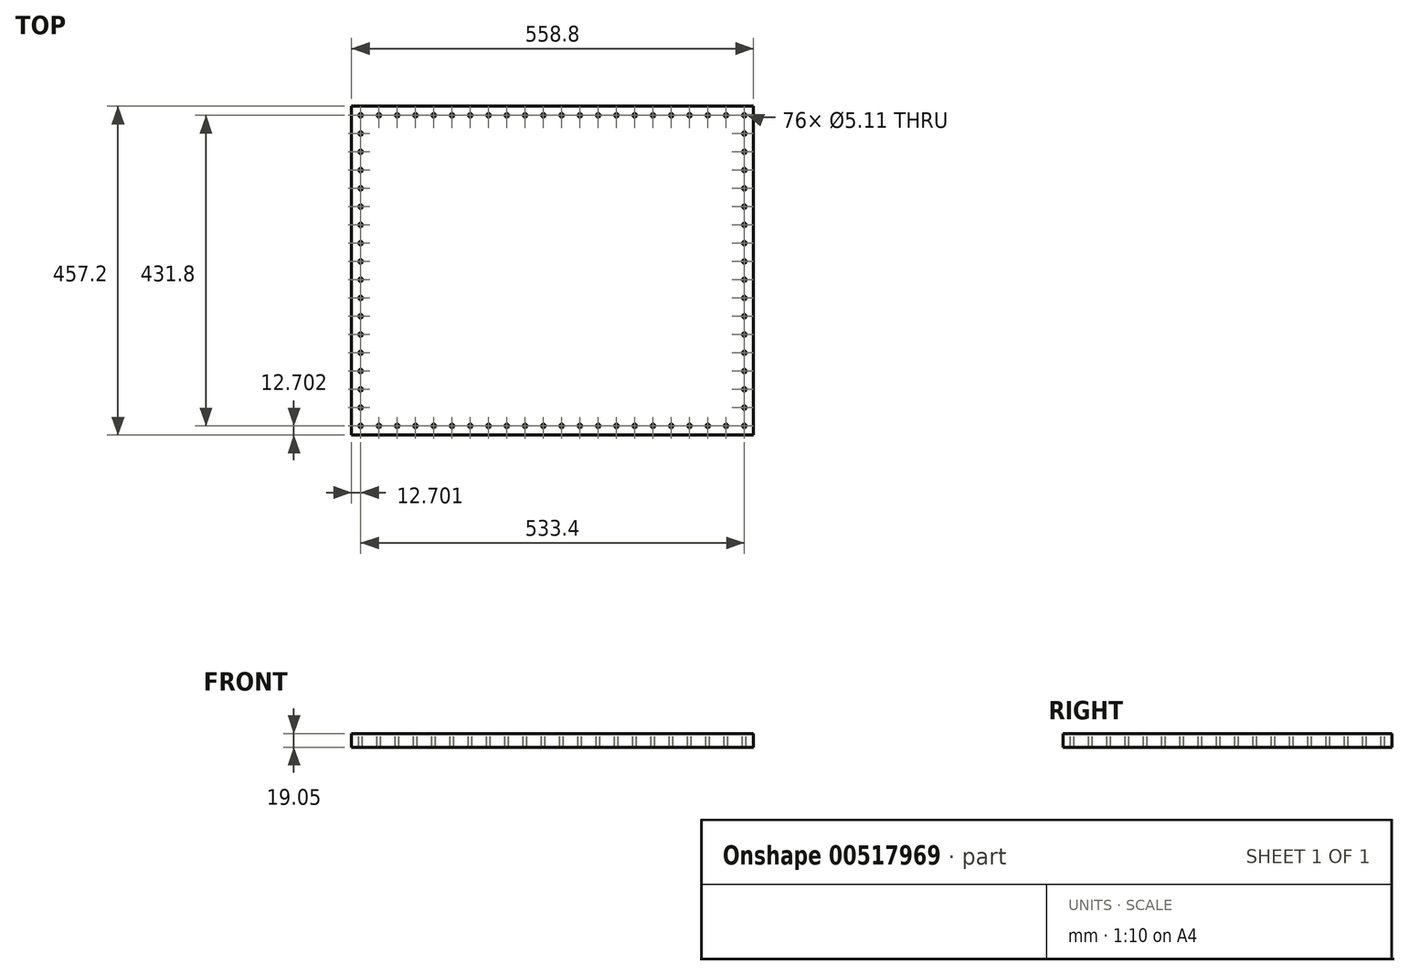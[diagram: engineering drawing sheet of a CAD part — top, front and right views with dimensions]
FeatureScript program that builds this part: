
annotation { "Feature Type Name" : "Feature", "Feature Type Description" : "" }
export const myFeature = defineFeature(function(context is Context, id is Id, definition is map)
    precondition{}
    {
        {
            var Q0;
            Q0=qCreatedBy(makeId("Top.planeOp"),FACE);
            var sketch = newSketch(context, id + "F0", { "sketchPlane" : qUnion([Q0])});
            skLineSegment(sketch, "E0.bottom", {"start": v(-249.54, 206.66) * mm, "end": v(309.26, 206.66) * mm});
            skLineSegment(sketch, "E0.top", {"start": v(-249.54, -250.54) * mm, "end": v(309.26, -250.54) * mm});
            skLineSegment(sketch, "E0.left", {"start": v(-249.54, 206.66) * mm, "end": v(-249.54, -250.54) * mm});
            skLineSegment(sketch, "E0.right", {"start": v(309.26, 206.66) * mm, "end": v(309.26, -250.54) * mm});
            skSolve(sketch);
        }
        {
            var Q0;
            Q0 = qSketchRegion(id + "F0", true);
            var Q1;
            Q1=makeQuery(id+"F0.imprint","IMPRINT",FACE,{"disambiguationData":[TD([[makeQuery(id+"F0.imprint","IMPRINT",EDGE,{"derivedFrom":sQuery(id+"F0.wireOp",EDGE,"E0.bottom")}),-1.0]])]});
            extrude(context, id + "F1", {"entities" : qUnion([Q0, Q1]), "depth" : 19.05 * mm, "offsetDistance" : 25.4 * mm});
        }
        {
            var Q0;
            Q0=makeQuery(id+"F1.opExtrude","CAP_FACE",FACE,{"disambiguationData":[OSD([sQuery(id+"F0.wireOp",EDGE,"E0.bottom"),sQuery(id+"F0.wireOp",EDGE,"E0.top"),sQuery(id+"F0.wireOp",EDGE,"E0.left"),sQuery(id+"F0.wireOp",EDGE,"E0.right")])],"isStart":false});
            var sketch = newSketch(context, id + "F2", { "sketchPlane" : qUnion([Q0])});
            skCircle(sketch, "E1", {"center": v(-236.84, 193.96) * mm, "radius": 2.55 * mm});
            skCircle(sketch, "E2.1.0.0", {"center": v(-211.44, 193.96) * mm, "radius": 2.55 * mm});
            skCircle(sketch, "E2.2.0.0", {"center": v(-186.04, 193.96) * mm, "radius": 2.55 * mm});
            skCircle(sketch, "E2.3.0.0", {"center": v(-160.64, 193.96) * mm, "radius": 2.55 * mm});
            skCircle(sketch, "E2.4.0.0", {"center": v(-135.24, 193.96) * mm, "radius": 2.55 * mm});
            skCircle(sketch, "E2.5.0.0", {"center": v(-109.84, 193.96) * mm, "radius": 2.55 * mm});
            skCircle(sketch, "E2.6.0.0", {"center": v(-84.44, 193.96) * mm, "radius": 2.55 * mm});
            skCircle(sketch, "E2.7.0.0", {"center": v(-59.04, 193.96) * mm, "radius": 2.55 * mm});
            skCircle(sketch, "E2.8.0.0", {"center": v(-33.64, 193.96) * mm, "radius": 2.55 * mm});
            skCircle(sketch, "E2.9.0.0", {"center": v(-8.24, 193.96) * mm, "radius": 2.55 * mm});
            skCircle(sketch, "E2.10.0.0", {"center": v(17.16, 193.96) * mm, "radius": 2.55 * mm});
            skCircle(sketch, "E2.11.0.0", {"center": v(42.56, 193.96) * mm, "radius": 2.55 * mm});
            skCircle(sketch, "E2.12.0.0", {"center": v(67.96, 193.96) * mm, "radius": 2.55 * mm});
            skCircle(sketch, "E2.13.0.0", {"center": v(93.36, 193.96) * mm, "radius": 2.55 * mm});
            skCircle(sketch, "E2.14.0.0", {"center": v(118.76, 193.96) * mm, "radius": 2.55 * mm});
            skCircle(sketch, "E2.15.0.0", {"center": v(144.16, 193.96) * mm, "radius": 2.55 * mm});
            skCircle(sketch, "E2.16.0.0", {"center": v(169.56, 193.96) * mm, "radius": 2.55 * mm});
            skCircle(sketch, "E2.17.0.0", {"center": v(194.96, 193.96) * mm, "radius": 2.55 * mm});
            skCircle(sketch, "E2.18.0.0", {"center": v(220.36, 193.96) * mm, "radius": 2.55 * mm});
            skCircle(sketch, "E2.19.0.0", {"center": v(245.76, 193.96) * mm, "radius": 2.55 * mm});
            skCircle(sketch, "E2.20.0.0", {"center": v(271.16, 193.96) * mm, "radius": 2.55 * mm});
            skCircle(sketch, "E2.21.0.0", {"center": v(296.56, 193.96) * mm, "radius": 2.55 * mm});
            skLineSegment(sketch, "E2.direction1", {"start": v(-236.84, 193.96) * mm, "end": v(-211.44, 193.96) * mm, "construction": true});
            skCircle(sketch, "E3.0.1.0", {"center": v(296.56, 168.56) * mm, "radius": 2.55 * mm});
            skCircle(sketch, "E3.0.2.0", {"center": v(296.56, 143.16) * mm, "radius": 2.55 * mm});
            skCircle(sketch, "E3.0.3.0", {"center": v(296.56, 117.76) * mm, "radius": 2.55 * mm});
            skCircle(sketch, "E3.0.4.0", {"center": v(296.56, 92.36) * mm, "radius": 2.55 * mm});
            skCircle(sketch, "E3.0.5.0", {"center": v(296.56, 66.96) * mm, "radius": 2.55 * mm});
            skCircle(sketch, "E3.0.6.0", {"center": v(296.56, 41.56) * mm, "radius": 2.55 * mm});
            skCircle(sketch, "E3.0.7.0", {"center": v(296.56, 16.16) * mm, "radius": 2.55 * mm});
            skCircle(sketch, "E3.0.8.0", {"center": v(296.56, -9.24) * mm, "radius": 2.55 * mm});
            skCircle(sketch, "E3.0.9.0", {"center": v(296.56, -34.64) * mm, "radius": 2.55 * mm});
            skCircle(sketch, "E3.0.10.0", {"center": v(296.56, -60.04) * mm, "radius": 2.55 * mm});
            skCircle(sketch, "E3.0.11.0", {"center": v(296.56, -85.44) * mm, "radius": 2.55 * mm});
            skCircle(sketch, "E3.0.12.0", {"center": v(296.56, -110.84) * mm, "radius": 2.55 * mm});
            skCircle(sketch, "E3.0.13.0", {"center": v(296.56, -136.24) * mm, "radius": 2.55 * mm});
            skCircle(sketch, "E3.0.14.0", {"center": v(296.56, -161.64) * mm, "radius": 2.55 * mm});
            skCircle(sketch, "E3.0.15.0", {"center": v(296.56, -187.04) * mm, "radius": 2.55 * mm});
            skCircle(sketch, "E3.0.16.0", {"center": v(296.56, -212.44) * mm, "radius": 2.55 * mm});
            skCircle(sketch, "E3.0.17.0", {"center": v(296.56, -237.84) * mm, "radius": 2.55 * mm});
            skLineSegment(sketch, "E3.direction1", {"start": v(296.56, 193.96) * mm, "end": v(321.96, 193.96) * mm, "construction": true});
            skLineSegment(sketch, "E3.direction2", {"start": v(296.56, 193.96) * mm, "end": v(296.56, 168.56) * mm, "construction": true});
            skCircle(sketch, "E4.1.0.0", {"center": v(271.16, -237.84) * mm, "radius": 2.55 * mm});
            skCircle(sketch, "E4.2.0.0", {"center": v(245.76, -237.84) * mm, "radius": 2.55 * mm});
            skCircle(sketch, "E4.3.0.0", {"center": v(220.36, -237.84) * mm, "radius": 2.55 * mm});
            skCircle(sketch, "E4.4.0.0", {"center": v(194.96, -237.84) * mm, "radius": 2.55 * mm});
            skCircle(sketch, "E4.5.0.0", {"center": v(169.56, -237.84) * mm, "radius": 2.55 * mm});
            skCircle(sketch, "E4.6.0.0", {"center": v(144.16, -237.84) * mm, "radius": 2.55 * mm});
            skCircle(sketch, "E4.7.0.0", {"center": v(118.76, -237.84) * mm, "radius": 2.55 * mm});
            skCircle(sketch, "E4.8.0.0", {"center": v(93.36, -237.84) * mm, "radius": 2.55 * mm});
            skCircle(sketch, "E4.9.0.0", {"center": v(67.96, -237.84) * mm, "radius": 2.55 * mm});
            skCircle(sketch, "E4.10.0.0", {"center": v(42.56, -237.84) * mm, "radius": 2.55 * mm});
            skCircle(sketch, "E4.11.0.0", {"center": v(17.16, -237.84) * mm, "radius": 2.55 * mm});
            skCircle(sketch, "E4.12.0.0", {"center": v(-8.24, -237.84) * mm, "radius": 2.55 * mm});
            skCircle(sketch, "E4.13.0.0", {"center": v(-33.64, -237.84) * mm, "radius": 2.55 * mm});
            skCircle(sketch, "E4.14.0.0", {"center": v(-59.04, -237.84) * mm, "radius": 2.55 * mm});
            skCircle(sketch, "E4.15.0.0", {"center": v(-84.44, -237.84) * mm, "radius": 2.55 * mm});
            skCircle(sketch, "E4.16.0.0", {"center": v(-109.84, -237.84) * mm, "radius": 2.55 * mm});
            skCircle(sketch, "E4.17.0.0", {"center": v(-135.24, -237.84) * mm, "radius": 2.55 * mm});
            skCircle(sketch, "E4.18.0.0", {"center": v(-160.64, -237.84) * mm, "radius": 2.55 * mm});
            skCircle(sketch, "E4.19.0.0", {"center": v(-186.04, -237.84) * mm, "radius": 2.55 * mm});
            skCircle(sketch, "E4.20.0.0", {"center": v(-211.44, -237.84) * mm, "radius": 2.55 * mm});
            skCircle(sketch, "E4.21.0.0", {"center": v(-236.84, -237.84) * mm, "radius": 2.55 * mm});
            skLineSegment(sketch, "E4.direction1", {"start": v(296.56, -237.84) * mm, "end": v(271.16, -237.84) * mm, "construction": true});
            skCircle(sketch, "E5.0.1.0", {"center": v(-236.84, -212.44) * mm, "radius": 2.55 * mm});
            skCircle(sketch, "E5.0.2.0", {"center": v(-236.84, -187.04) * mm, "radius": 2.55 * mm});
            skCircle(sketch, "E5.0.3.0", {"center": v(-236.84, -161.64) * mm, "radius": 2.55 * mm});
            skCircle(sketch, "E5.0.4.0", {"center": v(-236.84, -136.24) * mm, "radius": 2.55 * mm});
            skCircle(sketch, "E5.0.5.0", {"center": v(-236.84, -110.84) * mm, "radius": 2.55 * mm});
            skCircle(sketch, "E5.0.6.0", {"center": v(-236.84, -85.44) * mm, "radius": 2.55 * mm});
            skCircle(sketch, "E5.0.7.0", {"center": v(-236.84, -60.04) * mm, "radius": 2.55 * mm});
            skCircle(sketch, "E5.0.8.0", {"center": v(-236.84, -34.64) * mm, "radius": 2.55 * mm});
            skCircle(sketch, "E5.0.9.0", {"center": v(-236.84, -9.24) * mm, "radius": 2.55 * mm});
            skCircle(sketch, "E5.0.10.0", {"center": v(-236.84, 16.16) * mm, "radius": 2.55 * mm});
            skCircle(sketch, "E5.0.11.0", {"center": v(-236.84, 41.56) * mm, "radius": 2.55 * mm});
            skCircle(sketch, "E5.0.12.0", {"center": v(-236.84, 66.96) * mm, "radius": 2.55 * mm});
            skCircle(sketch, "E5.0.13.0", {"center": v(-236.84, 92.36) * mm, "radius": 2.55 * mm});
            skCircle(sketch, "E5.0.14.0", {"center": v(-236.84, 117.76) * mm, "radius": 2.55 * mm});
            skCircle(sketch, "E5.0.15.0", {"center": v(-236.84, 143.16) * mm, "radius": 2.55 * mm});
            skCircle(sketch, "E5.0.16.0", {"center": v(-236.84, 168.56) * mm, "radius": 2.55 * mm});
            skLineSegment(sketch, "E5.direction1", {"start": v(-236.84, -237.84) * mm, "end": v(-211.44, -237.84) * mm, "construction": true});
            skLineSegment(sketch, "E5.direction2", {"start": v(-236.84, -237.84) * mm, "end": v(-236.84, -212.44) * mm, "construction": true});
            skSolve(sketch);
        }
        {
            var Q0;
            Q0=sQuery(id+"F2.wireOp",VERTEX,"E5.0.8.0.center");
            var Q1;
            Q1=sQuery(id+"F2.wireOp",VERTEX,"E5.0.12.0.center");
            var Q2;
            Q2=sQuery(id+"F2.wireOp",VERTEX,"E2.15.0.0.center");
            var Q3;
            Q3=sQuery(id+"F2.wireOp",VERTEX,"E2.2.0.0.center");
            var Q4;
            Q4=sQuery(id+"F2.wireOp",VERTEX,"E3.0.14.0.center");
            var Q5;
            Q5=sQuery(id+"F2.wireOp",VERTEX,"E2.8.0.0.center");
            var Q6;
            Q6=sQuery(id+"F2.wireOp",VERTEX,"E4.8.0.0.center");
            var Q7;
            Q7=sQuery(id+"F2.wireOp",VERTEX,"E2.14.0.0.center");
            var Q8;
            Q8=sQuery(id+"F2.wireOp",VERTEX,"E4.2.0.0.center");
            var Q9;
            Q9=sQuery(id+"F2.wireOp",VERTEX,"E2.18.0.0.center");
            var Q10;
            Q10=sQuery(id+"F2.wireOp",VERTEX,"E2.13.0.0.center");
            var Q11;
            Q11=sQuery(id+"F2.wireOp",VERTEX,"E3.0.12.0.center");
            var Q12;
            Q12=sQuery(id+"F2.wireOp",VERTEX,"E3.0.3.0.center");
            var Q13;
            Q13=sQuery(id+"F2.wireOp",VERTEX,"E2.20.0.0.center");
            var Q14;
            Q14=sQuery(id+"F2.wireOp",VERTEX,"E4.15.0.0.center");
            var Q15;
            Q15=sQuery(id+"F2.wireOp",VERTEX,"E4.direction1.start");
            var Q16;
            Q16=sQuery(id+"F2.wireOp",VERTEX,"E3.0.8.0.center");
            var Q17;
            Q17=sQuery(id+"F2.wireOp",VERTEX,"E5.direction1.end");
            var Q18;
            Q18=sQuery(id+"F2.wireOp",VERTEX,"E4.11.0.0.center");
            var Q19;
            Q19=sQuery(id+"F2.wireOp",VERTEX,"E4.18.0.0.center");
            var Q20;
            Q20=sQuery(id+"F2.wireOp",VERTEX,"E3.0.2.0.center");
            var Q21;
            Q21=sQuery(id+"F2.wireOp",VERTEX,"E2.4.0.0.center");
            var Q22;
            Q22=sQuery(id+"F2.wireOp",VERTEX,"E2.17.0.0.center");
            var Q23;
            Q23=sQuery(id+"F2.wireOp",VERTEX,"E3.0.9.0.center");
            var Q24;
            Q24=sQuery(id+"F2.wireOp",VERTEX,"E5.0.6.0.center");
            var Q25;
            Q25=sQuery(id+"F2.wireOp",VERTEX,"E3.0.5.0.center");
            var Q26;
            Q26=sQuery(id+"F2.wireOp",VERTEX,"E4.17.0.0.center");
            var Q27;
            Q27=sQuery(id+"F2.wireOp",VERTEX,"E5.0.14.0.center");
            var Q28;
            Q28=sQuery(id+"F2.wireOp",VERTEX,"E2.10.0.0.center");
            var Q29;
            Q29=sQuery(id+"F2.wireOp",VERTEX,"E5.0.2.0.center");
            var Q30;
            Q30=sQuery(id+"F2.wireOp",VERTEX,"E5.0.15.0.center");
            var Q31;
            Q31=sQuery(id+"F2.wireOp",VERTEX,"E5.0.11.0.center");
            var Q32;
            Q32=sQuery(id+"F2.wireOp",VERTEX,"E5.0.10.0.center");
            var Q33;
            Q33=sQuery(id+"F2.wireOp",VERTEX,"E3.0.11.0.center");
            var Q34;
            Q34=sQuery(id+"F2.wireOp",VERTEX,"E2.11.0.0.center");
            var Q35;
            Q35=sQuery(id+"F2.wireOp",VERTEX,"E4.14.0.0.center");
            var Q36;
            Q36=sQuery(id+"F2.wireOp",VERTEX,"E5.0.13.0.center");
            var Q37;
            Q37=sQuery(id+"F2.wireOp",VERTEX,"E2.7.0.0.center");
            var Q38;
            Q38=sQuery(id+"F2.wireOp",VERTEX,"E4.1.0.0.center");
            var Q39;
            Q39=sQuery(id+"F2.wireOp",VERTEX,"E2.5.0.0.center");
            var Q40;
            Q40=sQuery(id+"F2.wireOp",VERTEX,"E5.0.3.0.center");
            var Q41;
            Q41=sQuery(id+"F2.wireOp",VERTEX,"E4.9.0.0.center");
            var Q42;
            Q42=sQuery(id+"F2.wireOp",VERTEX,"E3.0.10.0.center");
            var Q43;
            Q43=sQuery(id+"F2.wireOp",VERTEX,"E2.3.0.0.center");
            var Q44;
            Q44=sQuery(id+"F2.wireOp",VERTEX,"E4.5.0.0.center");
            var Q45;
            Q45=sQuery(id+"F2.wireOp",VERTEX,"E5.0.4.0.center");
            var Q46;
            Q46=sQuery(id+"F2.wireOp",VERTEX,"E5.direction2.end");
            var Q47;
            Q47=sQuery(id+"F2.wireOp",VERTEX,"E4.19.0.0.center");
            var Q48;
            Q48=sQuery(id+"F2.wireOp",VERTEX,"E4.12.0.0.center");
            var Q49;
            Q49=sQuery(id+"F2.wireOp",VERTEX,"E5.0.5.0.center");
            var Q50;
            Q50=sQuery(id+"F2.wireOp",VERTEX,"E4.7.0.0.center");
            var Q51;
            Q51=sQuery(id+"F2.wireOp",VERTEX,"E5.direction2.start");
            var Q52;
            Q52=sQuery(id+"F2.wireOp",VERTEX,"E4.13.0.0.center");
            var Q53;
            Q53=sQuery(id+"F2.wireOp",VERTEX,"E3.0.13.0.center");
            var Q54;
            Q54=sQuery(id+"F2.wireOp",VERTEX,"E3.0.6.0.center");
            var Q55;
            Q55=sQuery(id+"F2.wireOp",VERTEX,"E5.0.16.0.center");
            var Q56;
            Q56=sQuery(id+"F2.wireOp",VERTEX,"E2.direction1.end");
            var Q57;
            Q57=sQuery(id+"F2.wireOp",VERTEX,"E1.center");
            var Q58;
            Q58=sQuery(id+"F2.wireOp",VERTEX,"E2.16.0.0.center");
            var Q59;
            Q59=sQuery(id+"F2.wireOp",VERTEX,"E3.0.16.0.center");
            var Q60;
            Q60=sQuery(id+"F2.wireOp",VERTEX,"E4.3.0.0.center");
            var Q61;
            Q61=sQuery(id+"F2.wireOp",VERTEX,"E5.0.7.0.center");
            var Q62;
            Q62=sQuery(id+"F2.wireOp",VERTEX,"E4.16.0.0.center");
            var Q63;
            Q63=sQuery(id+"F2.wireOp",VERTEX,"E3.direction1.end");
            var Q64;
            Q64=sQuery(id+"F2.wireOp",VERTEX,"E2.6.0.0.center");
            var Q65;
            Q65=sQuery(id+"F2.wireOp",VERTEX,"E5.0.9.0.center");
            var Q66;
            Q66=sQuery(id+"F2.wireOp",VERTEX,"E2.19.0.0.center");
            var Q67;
            Q67=sQuery(id+"F2.wireOp",VERTEX,"E3.0.15.0.center");
            var Q68;
            Q68=sQuery(id+"F2.wireOp",VERTEX,"E3.direction2.start");
            var Q69;
            Q69=sQuery(id+"F2.wireOp",VERTEX,"E2.9.0.0.center");
            var Q70;
            Q70=sQuery(id+"F2.wireOp",VERTEX,"E4.6.0.0.center");
            var Q71;
            Q71=sQuery(id+"F2.wireOp",VERTEX,"E4.4.0.0.center");
            var Q72;
            Q72=sQuery(id+"F2.wireOp",VERTEX,"E3.direction2.end");
            var Q73;
            Q73=sQuery(id+"F2.wireOp",VERTEX,"E4.10.0.0.center");
            var Q74;
            Q74=sQuery(id+"F2.wireOp",VERTEX,"E2.12.0.0.center");
            var Q75;
            Q75=sQuery(id+"F2.wireOp",VERTEX,"E3.0.4.0.center");
            var Q76;
            Q76=sQuery(id+"F2.wireOp",VERTEX,"E3.0.7.0.center");
            var Q77;
            Q77=makeQuery(id+"F1.opExtrude","SWEPT_BODY",BODY,{"disambiguationData":[OSD([sQuery(id+"F0.wireOp",EDGE,"E0.bottom"),sQuery(id+"F0.wireOp",EDGE,"E0.top"),sQuery(id+"F0.wireOp",EDGE,"E0.left"),sQuery(id+"F0.wireOp",EDGE,"E0.right")])]});
            hole(context, id + "F3", {"style" : HoleStyle.SIMPLE, "endStyle" : HoleEndStyle.THROUGH, "holeDiameter" : 5.1 * mm, "isTappedThrough" : true, "tappedDepth" : 12.7 * mm, "tapClearance" : 3, "locations" : qUnion([Q0, Q1, Q2, Q3, Q4, Q5, Q6, Q7, Q8, Q9, Q10, Q11, Q12, Q13, Q14, Q15, Q16, Q17, Q18, Q19, Q20, Q21, Q22, Q23, Q24, Q25, Q26, Q27, Q28, Q29, Q30, Q31, Q32, Q33, Q34, Q35, Q36, Q37, Q38, Q39, Q40, Q41, Q42, Q43, Q44, Q45, Q46, Q47, Q48, Q49, Q50, Q51, Q52, Q53, Q54, Q55, Q56, Q57, Q58, Q59, Q60, Q61, Q62, Q63, Q64, Q65, Q66, Q67, Q68, Q69, Q70, Q71, Q72, Q73, Q74, Q75, Q76]), "scope" : qUnion([Q77])});
        }
    });
